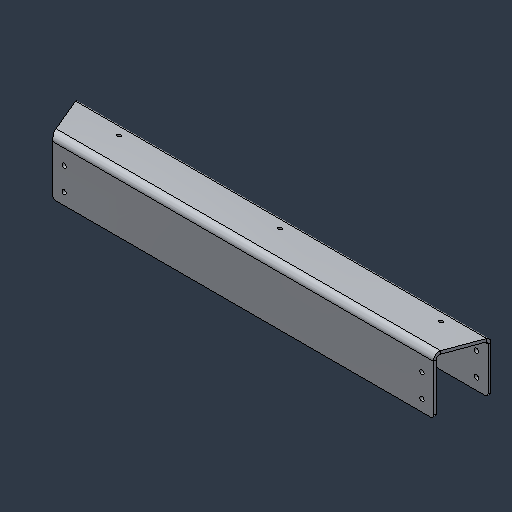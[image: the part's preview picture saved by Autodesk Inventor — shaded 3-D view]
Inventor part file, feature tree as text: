
AUTODESK INVENTOR PART (.ipt)
format: ipt  version: 2024.3 (Build 283343000, 343)  size: 143,360 bytes
history: native  units: mm (DEFAULTED — no unit token found)
features: fillet x1
ambient origin geometry x8: Origin, YZ Plane, XZ Plane, XY Plane, X Axis, Y Axis, Z Axis, Center Point
bodies: Solid1 (feature_tree)
feature tree (1):
  fillet  "Fillet1"  [1 undecoded]
note: 1 required parameter value undecoded (feature->parameter linkage not recoverable at this tier; creation-order binding heuristic only, values carry confidence <= 0.55)
